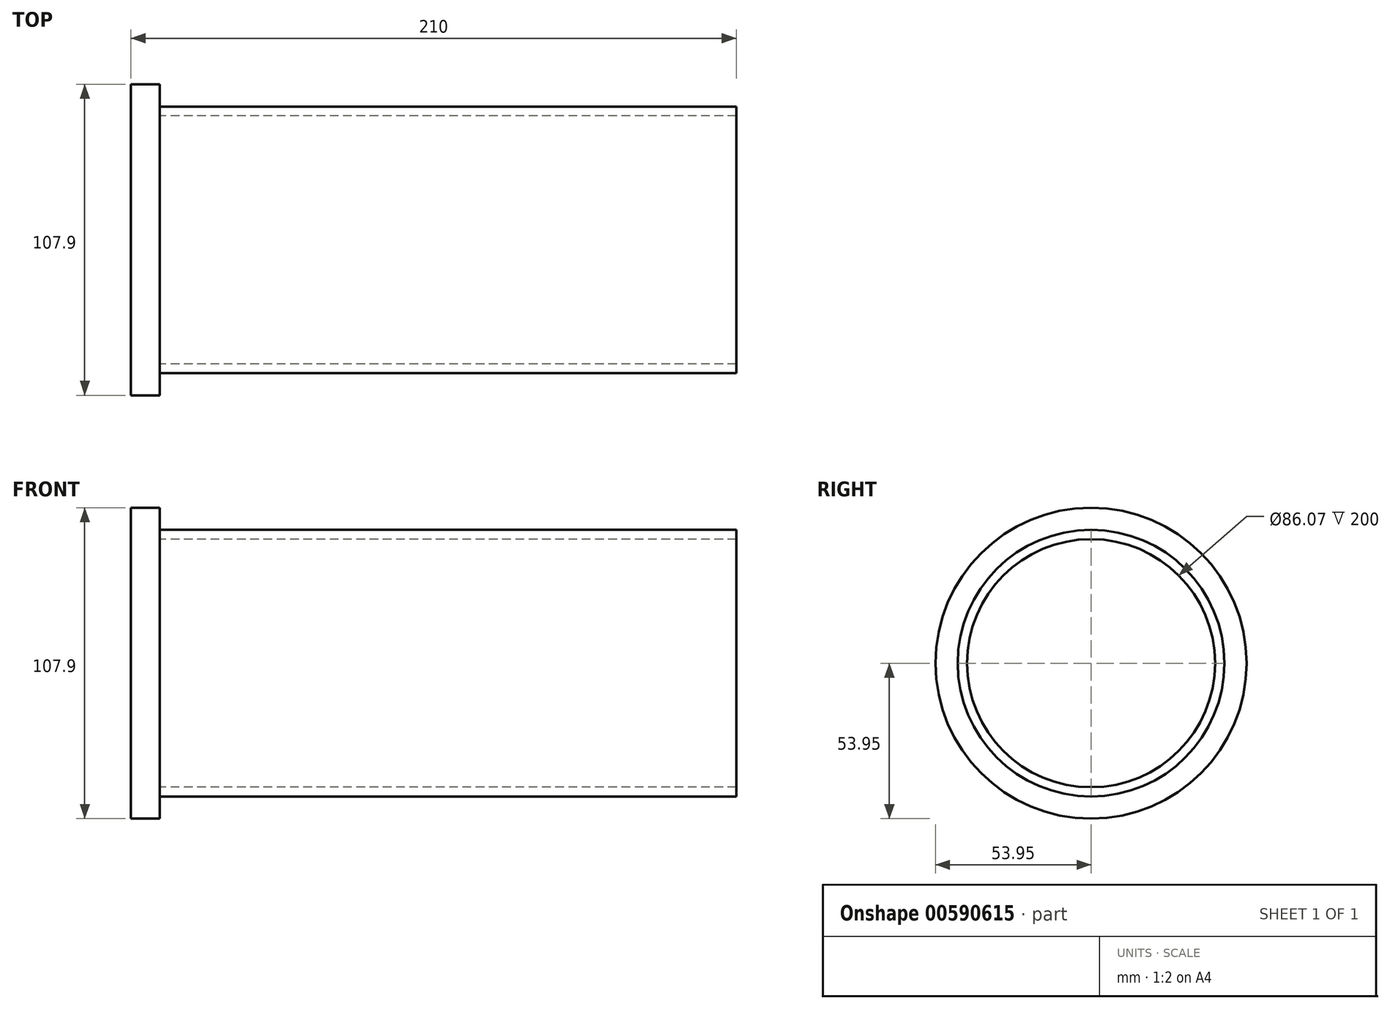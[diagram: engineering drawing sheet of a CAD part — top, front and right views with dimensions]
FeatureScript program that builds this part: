
annotation { "Feature Type Name" : "Feature", "Feature Type Description" : "" }
export const myFeature = defineFeature(function(context is Context, id is Id, definition is map)
    precondition{}
    {
        {
            var Q0;
            Q0=qCreatedBy(makeId("Right.planeOp"),FACE);
            var sketch = newSketch(context, id + "F0", { "sketchPlane" : qUnion([Q0])});
            skCircle(sketch, "E0", {"center": v(0, 0) * mm, "radius": 53.95 * mm});
            skSolve(sketch);
        }
        {
            var Q0;
            Q0=makeQuery(id+"F0.imprint","IMPRINT",FACE,{"disambiguationData":[TD([[makeQuery(id+"F0.imprint","IMPRINT",EDGE,{"derivedFrom":sQuery(id+"F0.wireOp",EDGE,"E0")}),1.0]])]});
            extrude(context, id + "F1", {"entities" : qUnion([Q0]), "depth" : 10 * mm, "offsetDistance" : 25.4 * mm});
        }
        {
            var Q0;
            Q0=makeQuery(id+"F1.opExtrude","CAP_FACE",FACE,{"disambiguationData":[OSD([sQuery(id+"F0.wireOp",EDGE,"E0")])],"isStart":false});
            var sketch = newSketch(context, id + "F2", { "sketchPlane" : qUnion([Q0])});
            skCircle(sketch, "E1", {"center": v(0, 0) * mm, "radius": 43.03 * mm});
            skCircle(sketch, "E2", {"center": v(0, 0) * mm, "radius": 46.26 * mm});
            skSolve(sketch);
        }
        {
            var Q0;
            Q0=makeQuery(id+"F2.imprint","IMPRINT",FACE,{"disambiguationData":[TD([[makeQuery(id+"F2.imprint","IMPRINT",EDGE,{"derivedFrom":sQuery(id+"F2.wireOp",EDGE,"E1")}),-1.0]])]});
            extrude(context, id + "F3", {"entities" : qUnion([Q0]), "operationType" : NewBodyOperationType.ADD, "depth" : 200 * mm, "offsetDistance" : 25 * mm});
        }
    });
